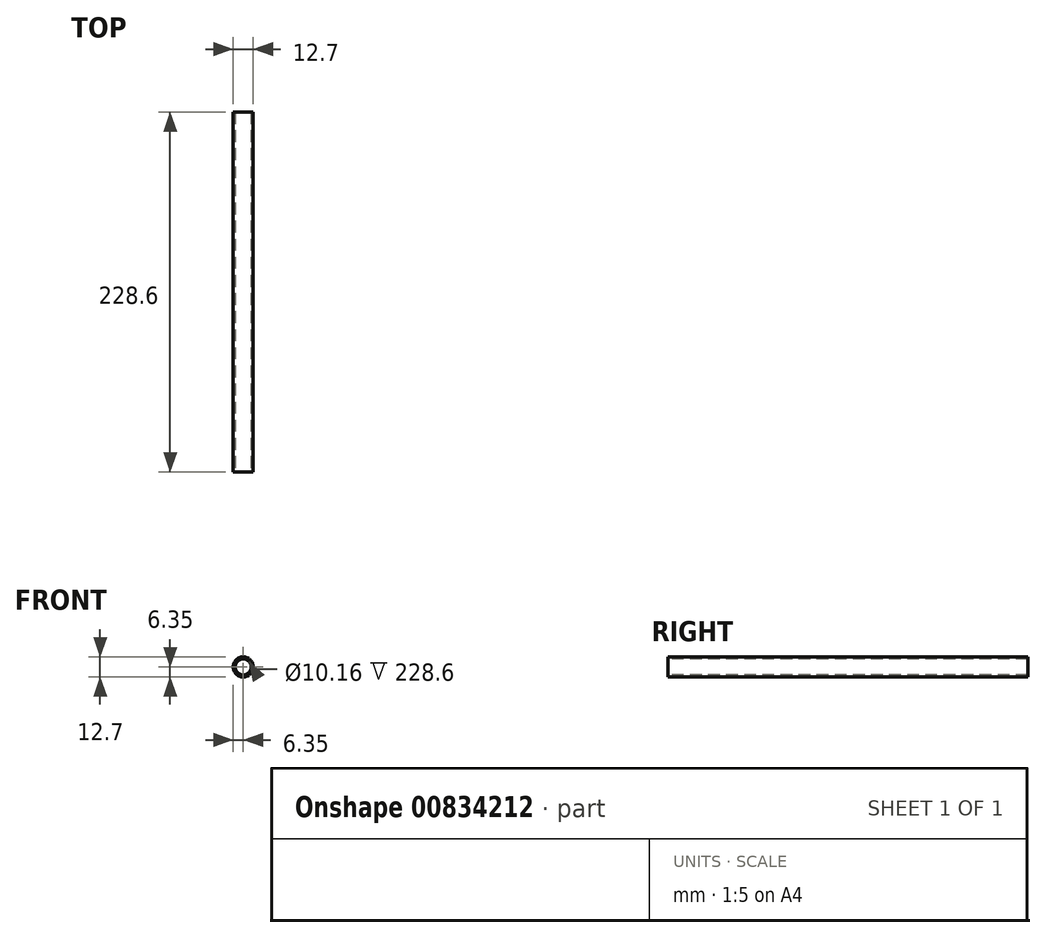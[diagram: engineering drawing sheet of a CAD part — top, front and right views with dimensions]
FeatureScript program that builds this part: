
annotation { "Feature Type Name" : "Feature", "Feature Type Description" : "" }
export const myFeature = defineFeature(function(context is Context, id is Id, definition is map)
    precondition{}
    {
        {
            var Q0;
            Q0=qCreatedBy(makeId("Front.planeOp"),FACE);
            var sketch = newSketch(context, id + "F0", { "sketchPlane" : qUnion([Q0])});
            skCircle(sketch, "E0", {"center": v(0, 0) * mm, "radius": 6.35 * mm});
            skCircle(sketch, "E1", {"center": v(0, 0) * mm, "radius": 5.08 * mm});
            skSolve(sketch);
        }
        {
            var Q0;
            Q0=makeQuery(id+"F0.imprint","IMPRINT",FACE,{"disambiguationData":[TD([[makeQuery(id+"F0.imprint","IMPRINT",EDGE,{"derivedFrom":sQuery(id+"F0.wireOp",EDGE,"E0")}),1.0]])]});
            extrude(context, id + "F1", {"entities" : qUnion([Q0]), "oppositeDirection" : true, "depth" : 228.6 * mm, "offsetDistance" : 25.4 * mm});
        }
    });
